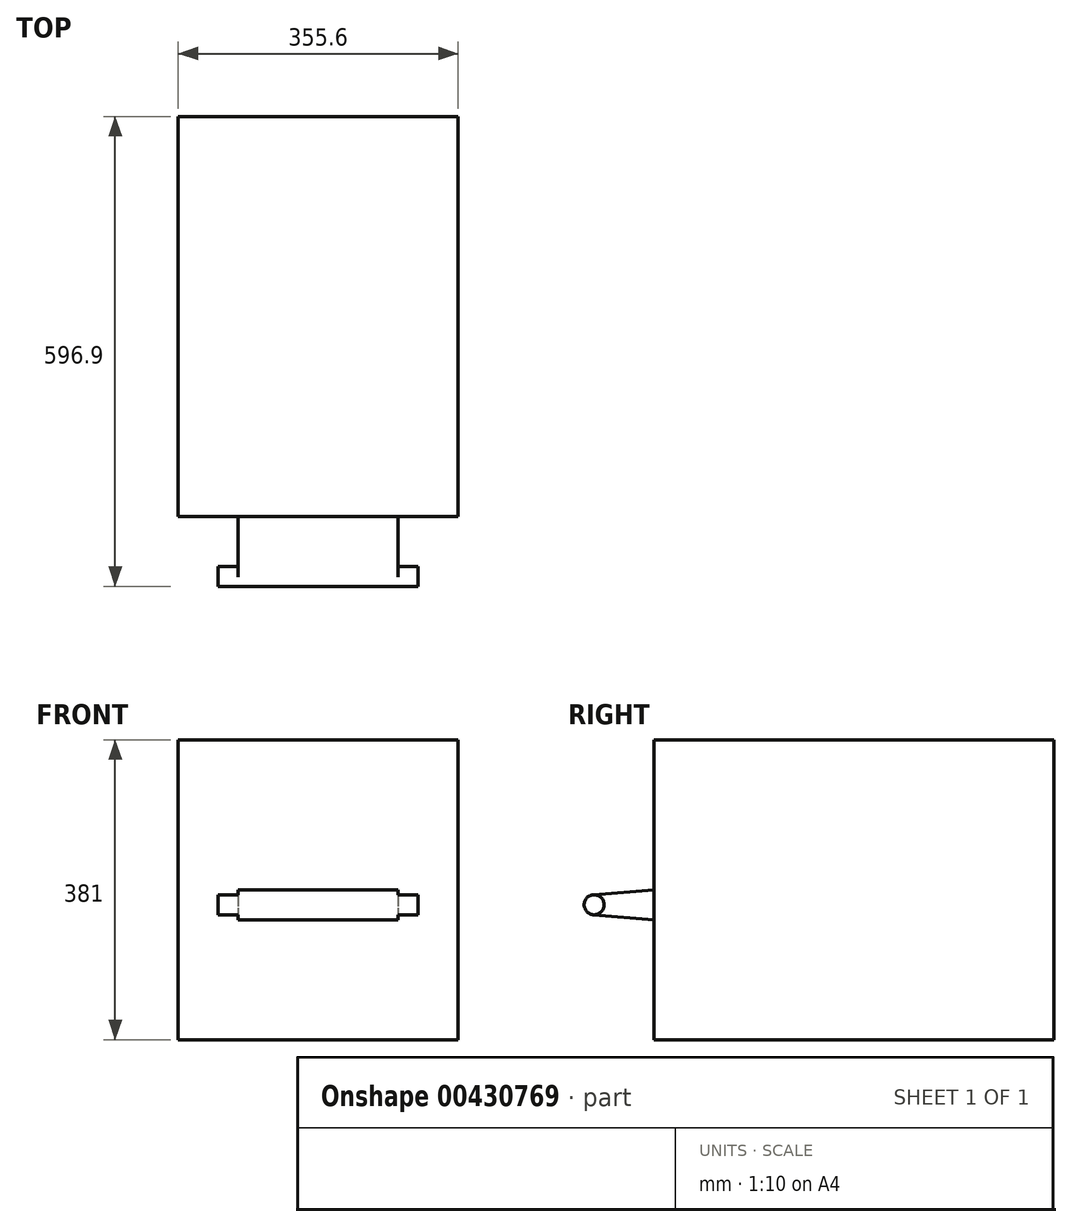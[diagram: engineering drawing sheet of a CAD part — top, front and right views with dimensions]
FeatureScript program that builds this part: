
annotation { "Feature Type Name" : "Feature", "Feature Type Description" : "" }
export const myFeature = defineFeature(function(context is Context, id is Id, definition is map)
    precondition{}
    {
        {
            var Q0;
            Q0=qCreatedBy(makeId("Top.planeOp"),FACE);
            var sketch = newSketch(context, id + "F0", { "sketchPlane" : qUnion([Q0])});
            skLineSegment(sketch, "E0.bottom", {"start": v(0, 0) * mm, "end": v(355.6, 0) * mm});
            skLineSegment(sketch, "E0.top", {"start": v(0, 508) * mm, "end": v(355.6, 508) * mm});
            skLineSegment(sketch, "E0.left", {"start": v(0, 0) * mm, "end": v(0, 508) * mm});
            skLineSegment(sketch, "E0.right", {"start": v(355.6, 0) * mm, "end": v(355.6, 508) * mm});
            skSolve(sketch);
        }
        {
            var Q0;
            Q0 = qSketchRegion(id + "F0", true);
            extrude(context, id + "F1", {"entities" : qUnion([Q0]), "depth" : 381 * mm});
        }
        {
            var Q0;
            Q0=makeQuery(id+"F1.opExtrude","SWEPT_FACE",FACE,{"disambiguationData":[OSD([sQuery(id+"F0.wireOp",EDGE,"E0.left")])]});
            var Q1;
            Q1=makeQuery(id+"F1.opExtrude","SWEPT_FACE",FACE,{"disambiguationData":[OSD([sQuery(id+"F0.wireOp",EDGE,"E0.right")])]});
            cPlane(context, id + "F2", {"entities" : qUnion([Q0, Q1]), "cplaneType" : CPlaneType.MID_PLANE, "offset" : 25.4 * mm, "width" : 152.4 * mm, "height" : 152.4 * mm});
        }
        {
            var Q0;
            Q0=qCreatedBy(id+"F2.planeOp",FACE);
            var sketch = newSketch(context, id + "F3", { "sketchPlane" : qUnion([Q0])});
            skCircle(sketch, "E1", {"center": v(76.2, 171.45) * mm, "radius": 12.7 * mm});
            skLineSegment(sketch, "E2", {"start": v(0, 190.5) * mm, "end": v(77.25, 184.1) * mm});
            skLineSegment(sketch, "E3", {"start": v(0, 152.4) * mm, "end": v(77.25, 158.8) * mm});
            skLineSegment(sketch, "E4", {"start": v(0, 190.5) * mm, "end": v(0, 152.4) * mm});
            skSolve(sketch);
        }
        {
            var Q0;
            {var subQ0=sQuery(id+"F3.wireOp",EDGE,"E2");Q0=makeQuery(id+"F3.imprint","IMPRINT",FACE,{"disambiguationData":[TD([[makeQuery(id+"F3.imprint","IMPRINT",EDGE,{"derivedFrom":subQ0}),-1.0]])]});}
            var Q1;
            Q1=makeQuery(id+"F1.opExtrude","SWEPT_FACE",FACE,{"disambiguationData":[OSD([sQuery(id+"F0.wireOp",EDGE,"E0.left")])]});
            var Q2;
            Q2=makeQuery(id+"F1.opExtrude","SWEPT_FACE",FACE,{"disambiguationData":[OSD([sQuery(id+"F0.wireOp",EDGE,"E0.right")])]});
            extrude(context, id + "F4", {"entities" : qUnion([Q0]), "operationType" : NewBodyOperationType.ADD, "endBoundEntityFace" : qUnion([Q1]), "depth" : 101.6 * mm, "hasSecondDirection" : true, "secondDirectionOppositeDirection" : true, "secondDirectionBoundEntityFace" : qUnion([Q2]), "secondDirectionDepth" : 101.6 * mm});
        }
        {
            var Q0;
            {var subQ0=sQuery(id+"F3.wireOp",EDGE,"E1");var subQ1=makeQuery(id+"F3.imprint","INTERSECT",VERTEX,{"derivedFrom":[subQ0,sQuery(id+"F3.wireOp",EDGE,"E2")]});Q0=makeQuery(id+"F3.imprint","IMPRINT",FACE,{"disambiguationData":[TD([[makeQuery(id+"F3.imprint","IMPRINT",EDGE,{"disambiguationData":[TD([[subQ1,-1.0]])],"derivedFrom":subQ0}),1.0]])]});}
            var Q1;
            Q1=makeQuery(id+"F1.opExtrude","SWEPT_FACE",FACE,{"disambiguationData":[OSD([sQuery(id+"F0.wireOp",EDGE,"E0.left")])]});
            var Q2;
            Q2=makeQuery(id+"F1.opExtrude","SWEPT_FACE",FACE,{"disambiguationData":[OSD([sQuery(id+"F0.wireOp",EDGE,"E0.right")])]});
            extrude(context, id + "F5", {"entities" : qUnion([Q0]), "operationType" : NewBodyOperationType.ADD, "endBoundEntityFace" : qUnion([Q1]), "depth" : 127 * mm, "hasSecondDirection" : true, "secondDirectionOppositeDirection" : true, "secondDirectionBoundEntityFace" : qUnion([Q2]), "secondDirectionDepth" : 127 * mm});
        }
    });
